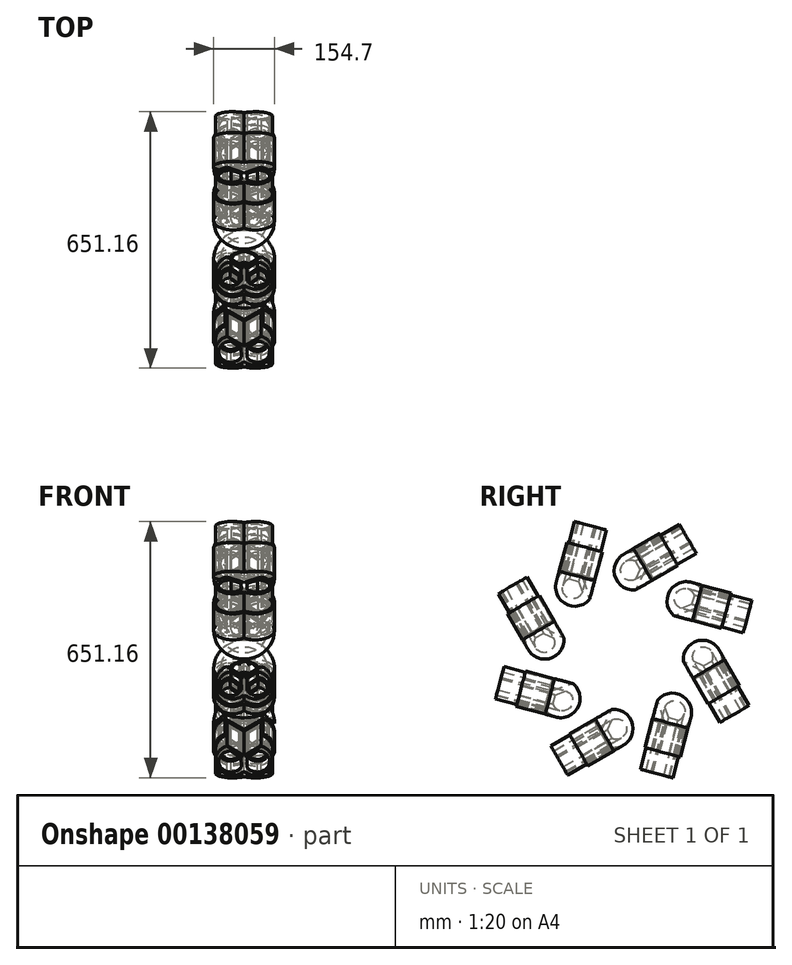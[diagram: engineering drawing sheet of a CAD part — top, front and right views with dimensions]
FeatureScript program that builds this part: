
annotation { "Feature Type Name" : "Feature", "Feature Type Description" : "" }
export const myFeature = defineFeature(function(context is Context, id is Id, definition is map)
    precondition{}
    {
        {
            var Q0;
            Q0=qCreatedBy(makeId("Right.planeOp"),FACE);
            var sketch = newSketch(context, id + "F0", { "sketchPlane" : qUnion([Q0])});
            skLineSegment(sketch, "E0", {"start": v(-45.46, 29.7) * mm, "end": v(0, 56) * mm});
            skLineSegment(sketch, "E1", {"start": v(0, 56) * mm, "end": v(51.6, 29.7) * mm});
            skArc(sketch, "E2", {"start": v(-45.46, 29.7) * mm, "mid": v(3.07, -24) * mm, "end": v(51.6, 29.7) * mm});
            skArc(sketch, "E3", {"start": v(-21.4, 29.7) * mm, "mid": v(1.93, -7.7) * mm, "end": v(25.25, 29.7) * mm});
            skLineSegment(sketch, "E4", {"start": v(-21.4, 29.7) * mm, "end": v(0, 41.13) * mm});
            skLineSegment(sketch, "E5", {"start": v(0, 41.13) * mm, "end": v(0, 41.13) * mm});
            skLineSegment(sketch, "E6", {"start": v(0, 41.13) * mm, "end": v(25.25, 29.7) * mm});
            skSolve(sketch);
        }
        {
            var Q0;
            Q0=makeQuery(id+"F0.imprint","IMPRINT",FACE,{"disambiguationData":[TD([[makeQuery(id+"F0.imprint","IMPRINT",EDGE,{"derivedFrom":sQuery(id+"F0.wireOp",EDGE,"E0")}),-1.0]])]});
            var Q1;
            Q1=sQuery(id+"F0.wireOp",EDGE,"E0");
            revolve(context, id + "F1", {"entities" : qUnion([Q0]), "axis" : qUnion([Q1]), "revolveType" : RevolveType.SYMMETRIC, "angle" : 180 * degree});
        }
        {
            var Q0;
            Q0=makeQuery(id+"F1.opRevolve","CAP_FACE",FACE,{"disambiguationData":[OSD([sQuery(id+"F0.wireOp",EDGE,"E0"),sQuery(id+"F0.wireOp",EDGE,"E1"),sQuery(id+"F0.wireOp",EDGE,"E2"),sQuery(id+"F0.wireOp",EDGE,"E3"),sQuery(id+"F0.wireOp",EDGE,"E4"),sQuery(id+"F0.wireOp",EDGE,"E6")])],"isStart":false});
            extrude(context, id + "F4", {"entities" : qUnion([Q0]), "depth" : 76.2 * mm});
        }
        {
            var Q0;
            {var subQ0=sQuery(id+"F0.wireOp",EDGE,"E1");Q0=makeQuery(id+"F4.opExtrude","SWEPT_FACE",FACE,{"disambiguationData":[OSD([subQ0]),TDD([makeQuery(id+"F1.opRevolve","CAP_EDGE",EDGE,{"disambiguationData":[OSD([subQ0])],"isStart":true})])]});}
            var Q1;
            {var subQ0=sQuery(id+"F0.wireOp",EDGE,"E1");Q1=makeQuery(id+"F4.opExtrude","SWEPT_FACE",FACE,{"disambiguationData":[OSD([subQ0]),TDD([makeQuery(id+"F1.opRevolve","CAP_EDGE",EDGE,{"disambiguationData":[OSD([subQ0])],"isStart":false})])]});}
            var Q2;
            Q2=makeQuery(id+"F4.opExtrude","CAP_FACE",FACE,{"disambiguationData":[OSD([sQuery(id+"F0.wireOp",EDGE,"E0"),sQuery(id+"F0.wireOp",EDGE,"E1"),sQuery(id+"F0.wireOp",EDGE,"E2"),sQuery(id+"F0.wireOp",EDGE,"E3"),sQuery(id+"F0.wireOp",EDGE,"E4"),sQuery(id+"F0.wireOp",EDGE,"E6")])],"isStart":false});
            shell(context, id + "F2", {"entities" : qUnion([Q0, Q1, Q2]), "thickness" : 5.08 * mm});
        }
        {
            var Q0;
            {var subQ0=sQuery(id+"F0.wireOp",EDGE,"E6");var subQ1=sQuery(id+"F0.wireOp",EDGE,"E4");var subQ2=sQuery(id+"F0.wireOp",EDGE,"E3");var subQ3=sQuery(id+"F0.wireOp",EDGE,"E2");var subQ4=sQuery(id+"F0.wireOp",EDGE,"E1");var subQ5=sQuery(id+"F0.wireOp",EDGE,"E0");Q0=makeQuery(id+"F2.opShell","OFFSET_FACE",FACE,{"disambiguationData":[OSD([subQ5,subQ4,subQ3,subQ2,subQ1,subQ0]),TDD([makeQuery(id+"F4.opExtrude","CAP_FACE",FACE,{"disambiguationData":[OSD([subQ5,subQ4,subQ3,subQ2,subQ1,subQ0])],"isStart":true})])]});}
            extrude(context, id + "F5", {"entities" : qUnion([Q0]), "depth" : 127 * mm});
        }
        {
            var Q0;
            {var subQ0=sQuery(id+"F0.wireOp",EDGE,"E1");Q0=makeQuery(id+"F4.opExtrude","SWEPT_FACE",FACE,{"disambiguationData":[OSD([subQ0]),TDD([makeQuery(id+"F1.opRevolve","CAP_EDGE",EDGE,{"disambiguationData":[OSD([subQ0])],"isStart":false})])]});}
            var Q1;
            {var subQ0=sQuery(id+"F0.wireOp",EDGE,"E2");var subQ1=sQuery(id+"F0.wireOp",EDGE,"E1");Q1=makeQuery(id+"F4.opExtrude","SWEPT_EDGE",EDGE,{"disambiguationData":[OSD([subQ1,subQ0]),TDD([makeQuery(id+"F1.opRevolve","CAP_VERTEX",VERTEX,{"disambiguationData":[OSD([subQ1,subQ0])],"isStart":true})])]});}
            revolve(context, id + "F6", {"entities" : qUnion([Q0]), "axis" : qUnion([Q1]), "revolveType" : RevolveType.ONE_DIRECTION, "angle" : 180 * degree});
        }
        {
            var Q0;
            Q0=makeQuery(id+"F6.opRevolve","SWEPT_BODY",BODY,{"disambiguationData":[OSD([sQuery(id+"F0.wireOp",EDGE,"E1")])]});
            deleteBodies(context, id + "F7", {"entities" : qUnion([Q0])});
        }
        {
            var Q0;
            Q0=qCreatedBy(makeId("Top.planeOp"),FACE);
            var sketch = newSketch(context, id + "F3", { "sketchPlane" : qUnion([Q0])});
            skLineSegment(sketch, "E7", {"start": v(-112.12, 203.3) * mm, "end": v(89.37, 203.3) * mm, "construction": true});
            skSolve(sketch);
        }
        {
            var Q0;
            Q0=makeQuery(id+"F5.opExtrude","SWEPT_BODY",BODY,{"disambiguationData":[OSD([sQuery(id+"F0.wireOp",EDGE,"E0"),sQuery(id+"F0.wireOp",EDGE,"E1"),sQuery(id+"F0.wireOp",EDGE,"E2"),sQuery(id+"F0.wireOp",EDGE,"E3"),sQuery(id+"F0.wireOp",EDGE,"E4"),sQuery(id+"F0.wireOp",EDGE,"E6")])]});
            var Q1;
            Q1=makeQuery(id+"F4.opExtrude","SWEPT_BODY",BODY,{"disambiguationData":[OSD([sQuery(id+"F0.wireOp",EDGE,"E0"),sQuery(id+"F0.wireOp",EDGE,"E1"),sQuery(id+"F0.wireOp",EDGE,"E2"),sQuery(id+"F0.wireOp",EDGE,"E3"),sQuery(id+"F0.wireOp",EDGE,"E4"),sQuery(id+"F0.wireOp",EDGE,"E6")])]});
            var Q2;
            Q2=makeQuery(id+"F1.opRevolve","SWEPT_BODY",BODY,{"disambiguationData":[OSD([sQuery(id+"F0.wireOp",EDGE,"E0"),sQuery(id+"F0.wireOp",EDGE,"E1"),sQuery(id+"F0.wireOp",EDGE,"E2"),sQuery(id+"F0.wireOp",EDGE,"E3"),sQuery(id+"F0.wireOp",EDGE,"E4"),sQuery(id+"F0.wireOp",EDGE,"E6")])]});
            var Q3;
            Q3=sQuery(id+"F3.wireOp",EDGE,"E7");
            circularPattern(context, id + "F8", {"entities" : qUnion([Q0, Q1, Q2]), "axis" : qUnion([Q3]), "angle" : 360 * degree, "instanceCount" : 8, "equalSpace" : true});
        }
    });
